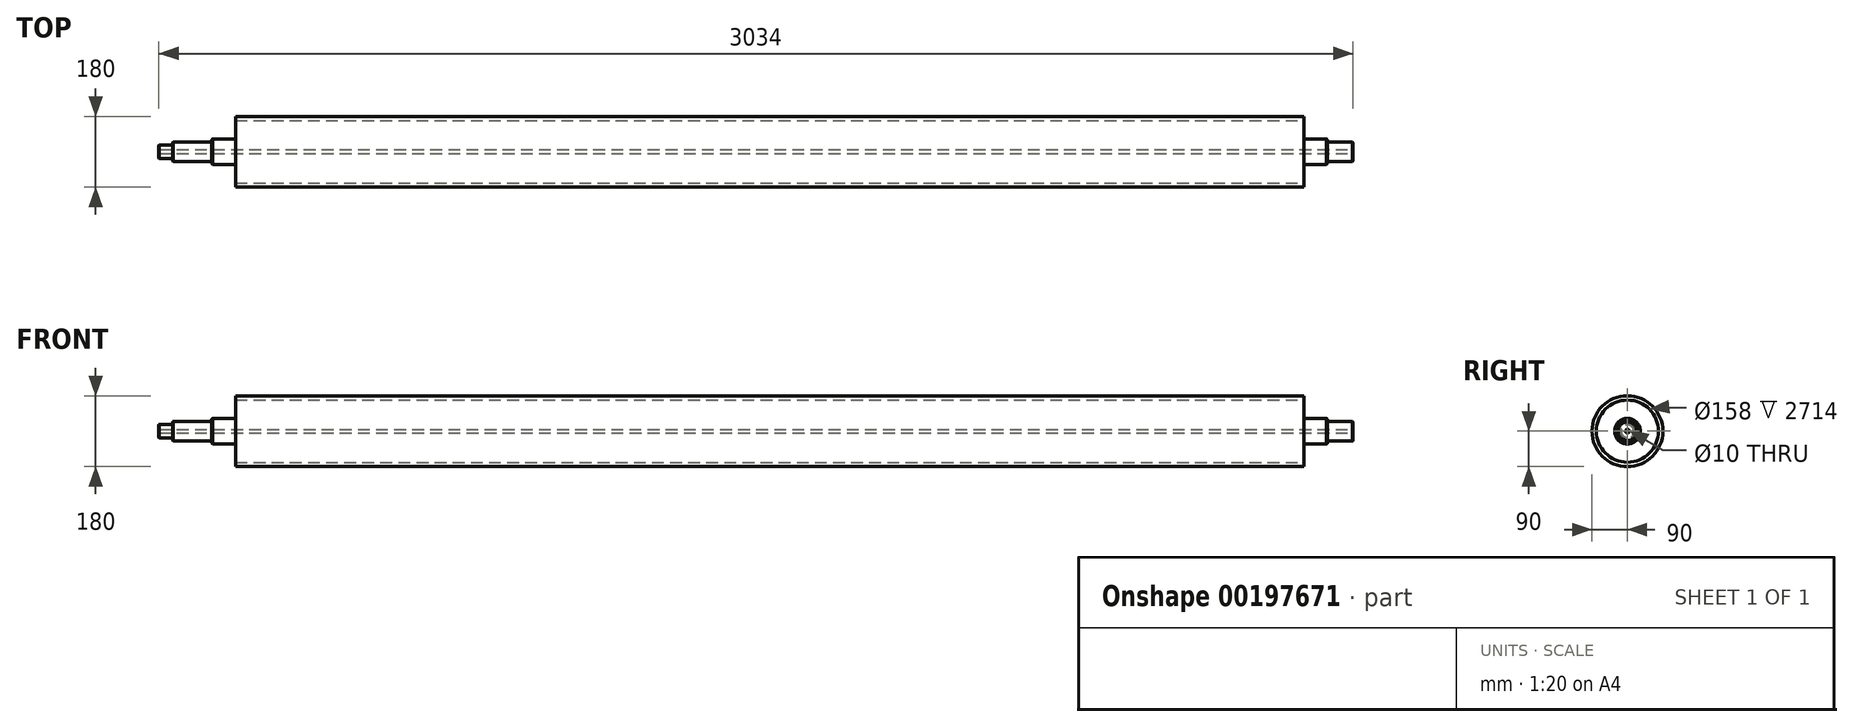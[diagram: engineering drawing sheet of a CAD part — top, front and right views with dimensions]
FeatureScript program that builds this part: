
annotation { "Feature Type Name" : "Feature", "Feature Type Description" : "" }
export const myFeature = defineFeature(function(context is Context, id is Id, definition is map)
    precondition{}
    {
        {
            var Q0;
            Q0=qCreatedBy(makeId("Right.planeOp"),FACE);
            var sketch = newSketch(context, id + "F0", { "sketchPlane" : qUnion([Q0])});
            skCircle(sketch, "E0", {"center": v(0, 0) * mm, "radius": 79 * mm});
            skSolve(sketch);
        }
        {
            var Q0;
            Q0 = qSketchRegion(id + "F0", true);
            extrude(context, id + "F1", {"entities" : qUnion([Q0]), "depth" : 2714 * mm, "symmetric" : true});
        }
        {
            var Q0;
            Q0=makeQuery(id+"F1.opExtrude","CAP_FACE",FACE,{"disambiguationData":[OSD([sQuery(id+"F0.wireOp",EDGE,"E0")])],"isStart":false});
            var sketch = newSketch(context, id + "F2", { "sketchPlane" : qUnion([Q0])});
            skCircle(sketch, "E1", {"center": v(0, 0) * mm, "radius": 32.5 * mm});
            skSolve(sketch);
        }
        {
            var Q0;
            Q0 = qSketchRegion(id + "F2", true);
            extrude(context, id + "F3", {"entities" : qUnion([Q0]), "operationType" : NewBodyOperationType.ADD, "depth" : 60 * mm});
        }
        {
            var Q0;
            Q0=makeQuery(id+"F3.opExtrude","CAP_EDGE",EDGE,{"disambiguationData":[OSD([sQuery(id+"F2.wireOp",EDGE,"E1")])],"isStart":false});
            chamfer(context, id + "F4", {"entities" : qUnion([Q0]), "width" : 2 * mm, "tangentPropagation" : true});
        }
        {
            var Q0;
            Q0=makeQuery(id+"F3.opExtrude","CAP_FACE",FACE,{"disambiguationData":[OSD([sQuery(id+"F2.wireOp",EDGE,"E1")])],"isStart":false});
            var sketch = newSketch(context, id + "F5", { "sketchPlane" : qUnion([Q0])});
            skCircle(sketch, "E2", {"center": v(0, 0) * mm, "radius": 25 * mm});
            skSolve(sketch);
        }
        {
            var Q0;
            Q0 = qSketchRegion(id + "F5", true);
            extrude(context, id + "F6", {"entities" : qUnion([Q0]), "operationType" : NewBodyOperationType.ADD, "depth" : 65 * mm});
        }
        {
            var Q0;
            Q0=makeQuery(id+"F6.opExtrude","CAP_EDGE",EDGE,{"disambiguationData":[OSD([sQuery(id+"F5.wireOp",EDGE,"E2")])],"isStart":false});
            chamfer(context, id + "F7", {"entities" : qUnion([Q0]), "width" : 1.5 * mm, "tangentPropagation" : true});
        }
        {
            var Q0;
            Q0=makeQuery(id+"F1.opExtrude","CAP_FACE",FACE,{"disambiguationData":[OSD([sQuery(id+"F0.wireOp",EDGE,"E0")])],"isStart":true});
            var sketch = newSketch(context, id + "F8", { "sketchPlane" : qUnion([Q0])});
            skCircle(sketch, "E3", {"center": v(0, 0) * mm, "radius": 32.5 * mm});
            skSolve(sketch);
        }
        {
            var Q0;
            Q0 = qSketchRegion(id + "F8", true);
            extrude(context, id + "F9", {"entities" : qUnion([Q0]), "operationType" : NewBodyOperationType.ADD, "depth" : 60 * mm});
        }
        {
            var Q0;
            Q0=makeQuery(id+"F9.opExtrude","CAP_FACE",FACE,{"disambiguationData":[OSD([sQuery(id+"F8.wireOp",EDGE,"E3")])],"isStart":false});
            var sketch = newSketch(context, id + "F10", { "sketchPlane" : qUnion([Q0])});
            skCircle(sketch, "E4", {"center": v(0, 0) * mm, "radius": 25 * mm});
            skSolve(sketch);
        }
        {
            var Q0;
            Q0 = qSketchRegion(id + "F10", true);
            extrude(context, id + "F11", {"entities" : qUnion([Q0]), "operationType" : NewBodyOperationType.ADD, "depth" : 100 * mm});
        }
        {
            var Q0;
            Q0=makeQuery(id+"F11.opExtrude","CAP_FACE",FACE,{"disambiguationData":[OSD([sQuery(id+"F10.wireOp",EDGE,"E4")])],"isStart":false});
            var sketch = newSketch(context, id + "F12", { "sketchPlane" : qUnion([Q0])});
            skCircle(sketch, "E5", {"center": v(0, 0) * mm, "radius": 17.5 * mm});
            skSolve(sketch);
        }
        {
            var Q0;
            Q0 = qSketchRegion(id + "F12", true);
            extrude(context, id + "F13", {"entities" : qUnion([Q0]), "operationType" : NewBodyOperationType.ADD, "depth" : 35 * mm});
        }
        {
            var Q0;
            Q0=makeQuery(id+"F9.opExtrude","CAP_EDGE",EDGE,{"disambiguationData":[OSD([sQuery(id+"F8.wireOp",EDGE,"E3")])],"isStart":false});
            chamfer(context, id + "F14", {"entities" : qUnion([Q0]), "width" : 2 * mm, "tangentPropagation" : true});
        }
        {
            var Q0;
            Q0=makeQuery(id+"F11.opExtrude","CAP_EDGE",EDGE,{"disambiguationData":[OSD([sQuery(id+"F10.wireOp",EDGE,"E4")])],"isStart":false});
            var Q1;
            Q1=makeQuery(id+"F13.opExtrude","CAP_EDGE",EDGE,{"disambiguationData":[OSD([sQuery(id+"F12.wireOp",EDGE,"E5")])],"isStart":false});
            chamfer(context, id + "F15", {"entities" : qUnion([Q0, Q1]), "width" : 1.5 * mm, "tangentPropagation" : true});
        }
        {
            var Q0;
            Q0=makeQuery(id+"F6.opExtrude","CAP_FACE",FACE,{"disambiguationData":[OSD([sQuery(id+"F5.wireOp",EDGE,"E2")])],"isStart":false});
            var sketch = newSketch(context, id + "F16", { "sketchPlane" : qUnion([Q0])});
            skCircle(sketch, "E6", {"center": v(0, 0) * mm, "radius": 5 * mm});
            skSolve(sketch);
        }
        {
            var Q0;
            Q0 = qSketchRegion(id + "F16", true);
            extrude(context, id + "F17", {"entities" : qUnion([Q0]), "operationType" : NewBodyOperationType.REMOVE, "endBound" : BoundingType.THROUGH_ALL, "oppositeDirection" : true, "depth" : 25 * mm});
        }
        {
            var Q0;
            Q0=makeQuery(id+"F1.opExtrude","CAP_FACE",FACE,{"disambiguationData":[OSD([sQuery(id+"F0.wireOp",EDGE,"E0")])],"isStart":false});
            var sketch = newSketch(context, id + "F18", { "sketchPlane" : qUnion([Q0])});
            skCircle(sketch, "E7", {"center": v(0, 0) * mm, "radius": 90 * mm});
            skCircle(sketch, "E8.0", {"center": v(0, 0) * mm, "radius": 79 * mm});
            skSolve(sketch);
        }
        {
            var Q0;
            Q0 = qSketchRegion(id + "F18", true);
            var Q1;
            Q1=makeQuery(id+"F1.opExtrude","CAP_FACE",FACE,{"disambiguationData":[OSD([sQuery(id+"F0.wireOp",EDGE,"E0")])],"isStart":true});
            extrude(context, id + "F19", {"entities" : qUnion([Q0]), "endBound" : BoundingType.UP_TO_SURFACE, "oppositeDirection" : true, "endBoundEntityFace" : qUnion([Q1]), "depth" : 25 * mm});
        }
    });
